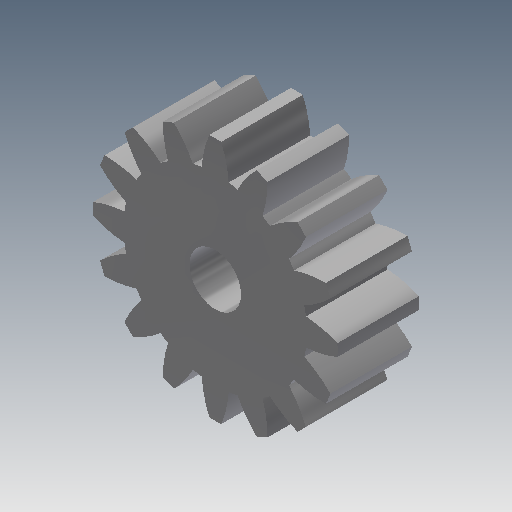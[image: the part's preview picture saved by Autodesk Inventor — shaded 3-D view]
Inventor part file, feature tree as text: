
AUTODESK INVENTOR PART (.ipt)
format: ipt  version: 2019.4 (Build 234330000, 330)  size: 218,624 bytes
history: native  units: mm (DEFAULTED — no unit token found)
features: other x5, plane x3, sketch x2, extrude x1, reference x1
ambient origin geometry x8: Origin, YZ Plane, XZ Plane, XY Plane, X Axis, Y Axis, Z Axis, Center Point
bodies: Solid1 (feature_tree)
feature tree (12):
  extrude  "Extrusion1"  Depth=6.0mm TaperAngle=0.0deg
  plane  "Work Plane2"
  plane  "Work Plane8"
  plane  "Work Plane9"
  other  "Spur Gear"
  sketch  "Sketch1"  dims[d0=18.0mm d1=6.0mm d2=0.0mm]
  sketch  "Sketch2"  dims[d3=16.0mm d4=10.0mm d5=0.0mm d16=13.0mm d17=0.0mm d34=1.963495mm d39=0.0mm d41=0.0mm d43=13.0mm d46=13.0mm d47=0.0mm d48=0.0mm d49=3.8mm]
  other  "Srf1"
  reference  "Reference1"
  other  "Pitch Diameter"
  other  "Assembly_Opentrons_Autofocus_v2.iam"
  other  "DIN 912 - replaced by DIN EN ISO 4762 M4 x 20:1"
